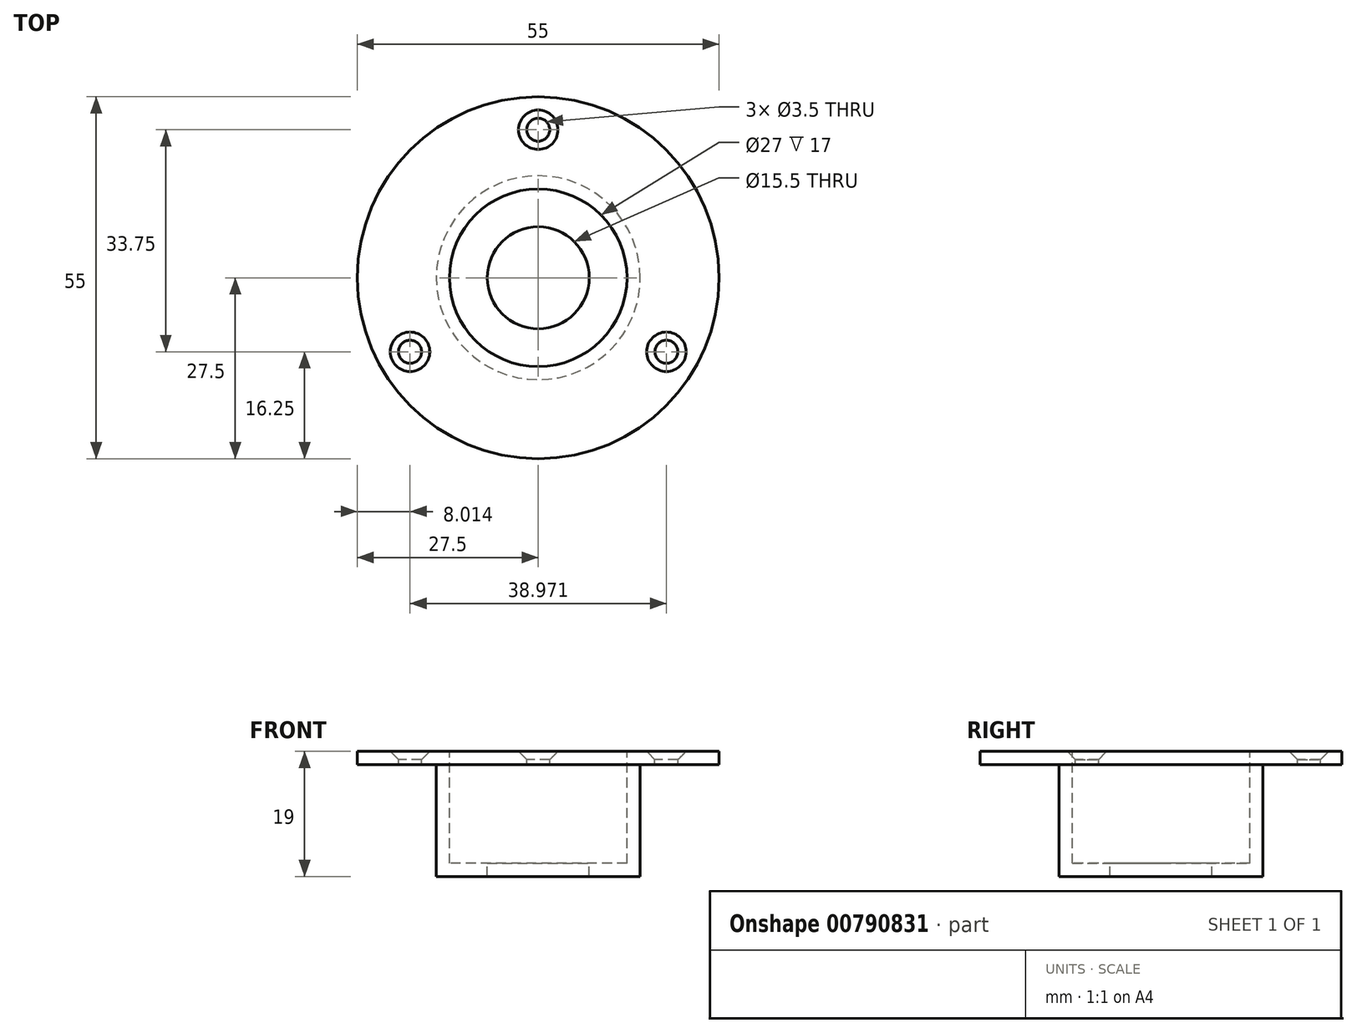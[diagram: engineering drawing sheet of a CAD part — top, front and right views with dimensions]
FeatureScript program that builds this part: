
annotation { "Feature Type Name" : "Feature", "Feature Type Description" : "" }
export const myFeature = defineFeature(function(context is Context, id is Id, definition is map)
    precondition{}
    {
        {
            var Q0;
            Q0=qCreatedBy(makeId("Top.planeOp"),FACE);
            var sketch = newSketch(context, id + "F0", { "sketchPlane" : qUnion([Q0])});
            skCircle(sketch, "E0", {"center": v(0, 0) * mm, "radius": 13.5 * mm});
            skCircle(sketch, "E1.0", {"center": v(0, 0) * mm, "radius": 15.5 * mm});
            skSolve(sketch);
        }
        {
            var Q0;
            Q0=makeQuery(id+"F0.imprint","IMPRINT",FACE,{"disambiguationData":[TD([[makeQuery(id+"F0.imprint","IMPRINT",EDGE,{"derivedFrom":sQuery(id+"F0.wireOp",EDGE,"E0")}),-1.0]])]});
            extrude(context, id + "F1", {"entities" : qUnion([Q0]), "depth" : -15 * mm, "offsetDistance" : 25 * mm});
        }
        {
            var Q0;
            Q0=qCreatedBy(makeId("Top.planeOp"),FACE);
            var sketch = newSketch(context, id + "F2", { "sketchPlane" : qUnion([Q0])});
            skCircle(sketch, "E2", {"center": v(0, 0) * mm, "radius": 13.5 * mm});
            skCircle(sketch, "E3", {"center": v(0, 0) * mm, "radius": 27.5 * mm});
            skSolve(sketch);
        }
        {
            var Q0;
            Q0=qSketchRegion(id+"F2",true);
            extrude(context, id + "F3", {"entities" : qUnion([Q0]), "operationType" : NewBodyOperationType.ADD, "depth" : 2 * mm, "offsetDistance" : 25 * mm});
        }
        {
            var Q0;
            Q0=makeQuery(id+"F1.opExtrude","CAP_FACE",FACE,{"disambiguationData":[OSD([sQuery(id+"F0.wireOp",EDGE,"E0"),sQuery(id+"F0.wireOp",EDGE,"E1.0")])],"isStart":false});
            var sketch = newSketch(context, id + "F4", { "sketchPlane" : qUnion([Q0])});
            skCircle(sketch, "E4", {"center": v(0, 0) * mm, "radius": 15.5 * mm});
            skCircle(sketch, "E5", {"center": v(0, 0) * mm, "radius": 7.75 * mm});
            skSolve(sketch);
        }
        {
            var Q0;
            Q0=qSketchRegion(id+"F4",true);
            extrude(context, id + "F5", {"entities" : qUnion([Q0]), "operationType" : NewBodyOperationType.ADD, "depth" : 2 * mm, "offsetDistance" : 25 * mm});
        }
        {
            var Q0;
            Q0=makeQuery(id+"F3.opExtrude","CAP_FACE",FACE,{"disambiguationData":[OSD([sQuery(id+"F2.wireOp",EDGE,"E2"),sQuery(id+"F2.wireOp",EDGE,"E3")])],"isStart":false});
            var sketch = newSketch(context, id + "F6", { "sketchPlane" : qUnion([Q0])});
            skCircle(sketch, "E6", {"center": v(0, 0) * mm, "radius": 22.5 * mm});
            skCircle(sketch, "E7", {"center": v(0, 22.5) * mm, "radius": 1.75 * mm});
            skCircle(sketch, "E8.1.0", {"center": v(-19.49, -11.25) * mm, "radius": 1.75 * mm});
            skCircle(sketch, "E8.2.0", {"center": v(19.49, -11.25) * mm, "radius": 1.75 * mm});
            skSolve(sketch);
        }
        {
            var Q0;
            Q0=sQuery(id+"F6.wireOp",VERTEX,"E7.center");
            var Q1;
            Q1=sQuery(id+"F6.wireOp",VERTEX,"E8.1.0.center");
            var Q2;
            Q2=sQuery(id+"F6.wireOp",VERTEX,"E8.2.0.center");
            var Q3;
            Q3=makeQuery(id+"F1.opExtrude","SWEPT_BODY",BODY,{"disambiguationData":[OSD([sQuery(id+"F0.wireOp",EDGE,"E0"),sQuery(id+"F0.wireOp",EDGE,"E1.0")])]});
            hole(context, id + "F7", {"style" : HoleStyle.C_SINK, "endStyle" : HoleEndStyle.THROUGH, "holeDiameter" : 3.5 * mm, "cSinkDiameter" : 6 * mm, "cSinkAngle" : 90 * degree, "majorDiameter" : 5 * mm, "isTappedThrough" : true, "tappedDepth" : 12 * mm, "tapClearance" : 3, "locations" : qUnion([Q0, Q1, Q2]), "scope" : qUnion([Q3])});
        }
    });
